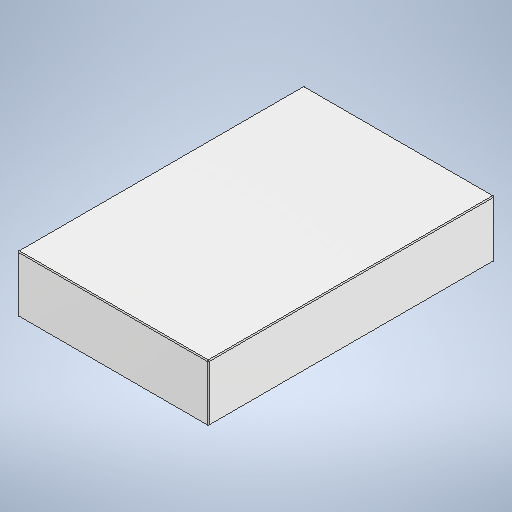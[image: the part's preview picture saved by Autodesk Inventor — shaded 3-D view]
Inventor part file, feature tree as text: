
AUTODESK INVENTOR PART (.ipt)
format: ipt  version: 2025 (Build 290162000, 162)  size: 222,720 bytes
history: native  units: in
note: dims shown in document units (in); Inventor stores cm internally (conversion verified against a paired STEP export)
features: extrude x1, fillet x1, sketch x1, other x1
ambient origin geometry x8: Origin, YZ Plane, XZ Plane, XY Plane, X Axis, Y Axis, Z Axis, Center Point
bodies: Solid1 (feature_tree)
feature tree (4):
  extrude  "Extrusion1"  Depth=15.748in
  fillet  "Fillet1"  Radius=23.622in
  sketch  "Sketch1"  dims[d0=4.685in d1=15.748in d2=23.622in d3=0.0in d4=0.0787in]
  other  "Finish1"
